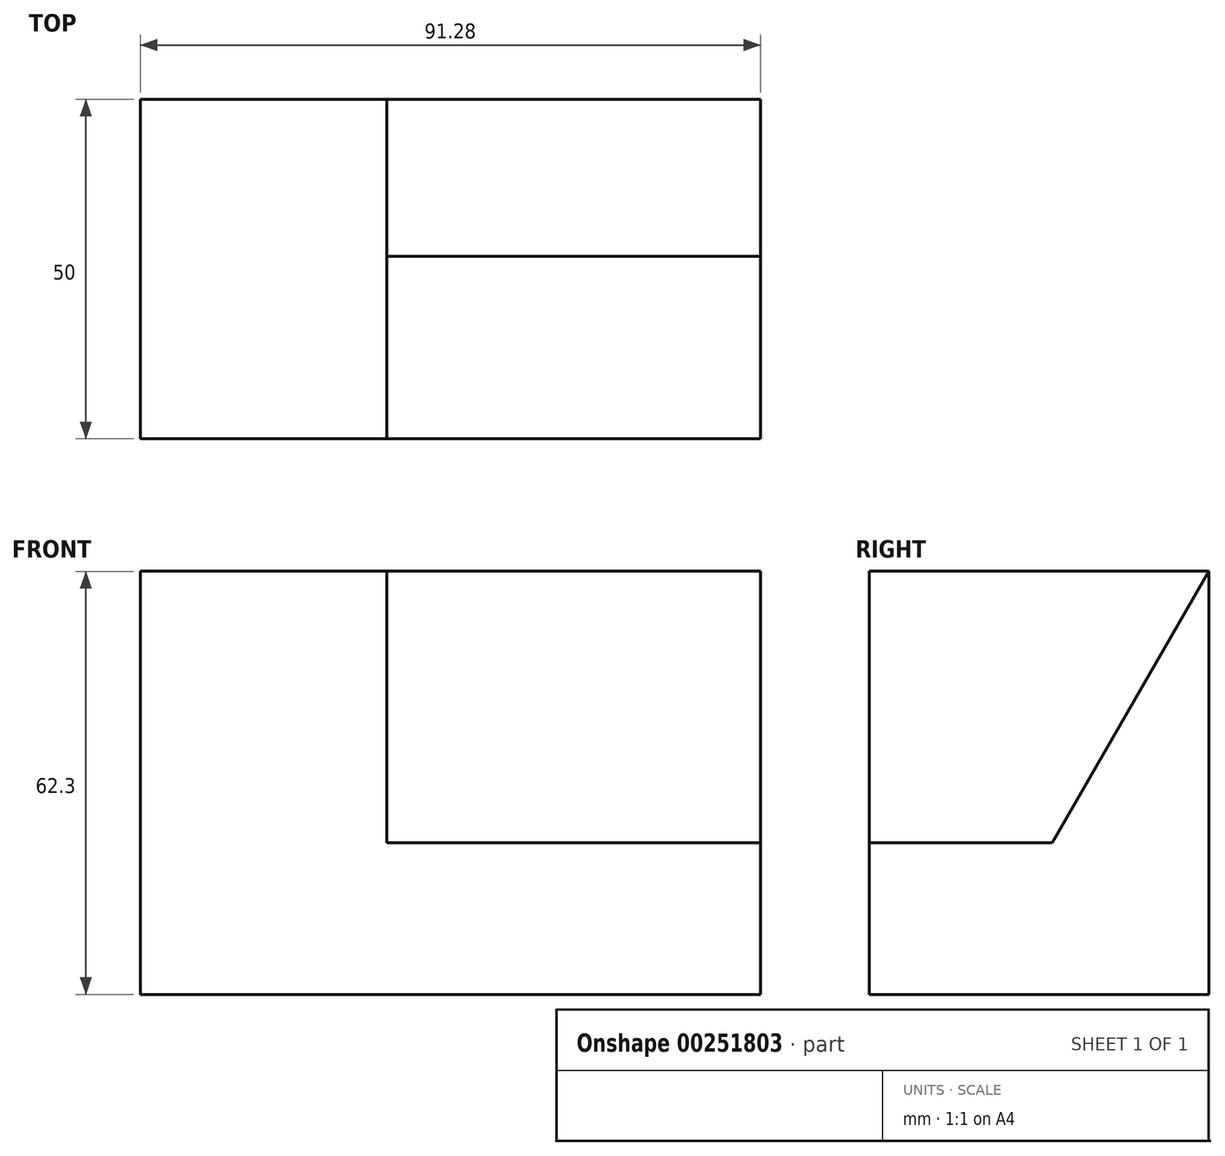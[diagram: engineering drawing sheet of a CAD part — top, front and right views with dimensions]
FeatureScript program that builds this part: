
annotation { "Feature Type Name" : "Feature", "Feature Type Description" : "" }
export const myFeature = defineFeature(function(context is Context, id is Id, definition is map)
    precondition{}
    {
        {
            var Q0;
            Q0=qCreatedBy(makeId("Front.planeOp"),FACE);
            var sketch = newSketch(context, id + "F0", { "sketchPlane" : qUnion([Q0])});
            skLineSegment(sketch, "E0.bottom", {"start": v(-45.64, 31.15) * mm, "end": v(45.64, 31.15) * mm});
            skLineSegment(sketch, "E0.top", {"start": v(-45.64, -31.15) * mm, "end": v(45.64, -31.15) * mm});
            skLineSegment(sketch, "E0.left", {"start": v(-45.64, 31.15) * mm, "end": v(-45.64, -31.15) * mm});
            skLineSegment(sketch, "E0.right", {"start": v(45.64, 31.15) * mm, "end": v(45.64, -31.15) * mm});
            skPoint(sketch, "E0.middle", {"position": v(0, 0) * mm});
            skSolve(sketch);
        }
        {
            var Q0;
            Q0=makeQuery(id+"F0.imprint","IMPRINT",FACE,{"disambiguationData":[TD([[makeQuery(id+"F0.imprint","IMPRINT",EDGE,{"derivedFrom":sQuery(id+"F0.wireOp",EDGE,"E0.bottom")}),-1.0]])]});
            extrude(context, id + "F1", {"entities" : qUnion([Q0]), "oppositeDirection" : true, "depth" : 50 * mm});
        }
        {
            var Q0;
            Q0=makeQuery(id+"F1.opExtrude","SWEPT_FACE",FACE,{"disambiguationData":[OSD([sQuery(id+"F0.wireOp",EDGE,"E0.right")])]});
            var sketch = newSketch(context, id + "F2", { "sketchPlane" : qUnion([Q0])});
            skLineSegment(sketch, "E1", {"start": v(0, -8.85) * mm, "end": v(26.9, -8.85) * mm});
            skLineSegment(sketch, "E2", {"start": v(26.9, -8.85) * mm, "end": v(50, 31.15) * mm});
            skLineSegment(sketch, "E3.0", {"start": v(50, 31.15) * mm, "end": v(0, 31.15) * mm});
            skLineSegment(sketch, "E4.0", {"start": v(0, 31.15) * mm, "end": v(0, -8.85) * mm});
            skPoint(sketch, "E5.orphan", {"position": v(0, -31.15) * mm});
            skSolve(sketch);
        }
        {
            var Q0;
            Q0 = qSketchRegion(id + "F2", true);
            extrude(context, id + "F3", {"entities" : qUnion([Q0]), "operationType" : NewBodyOperationType.REMOVE, "oppositeDirection" : true, "depth" : 55 * mm});
        }
    });
